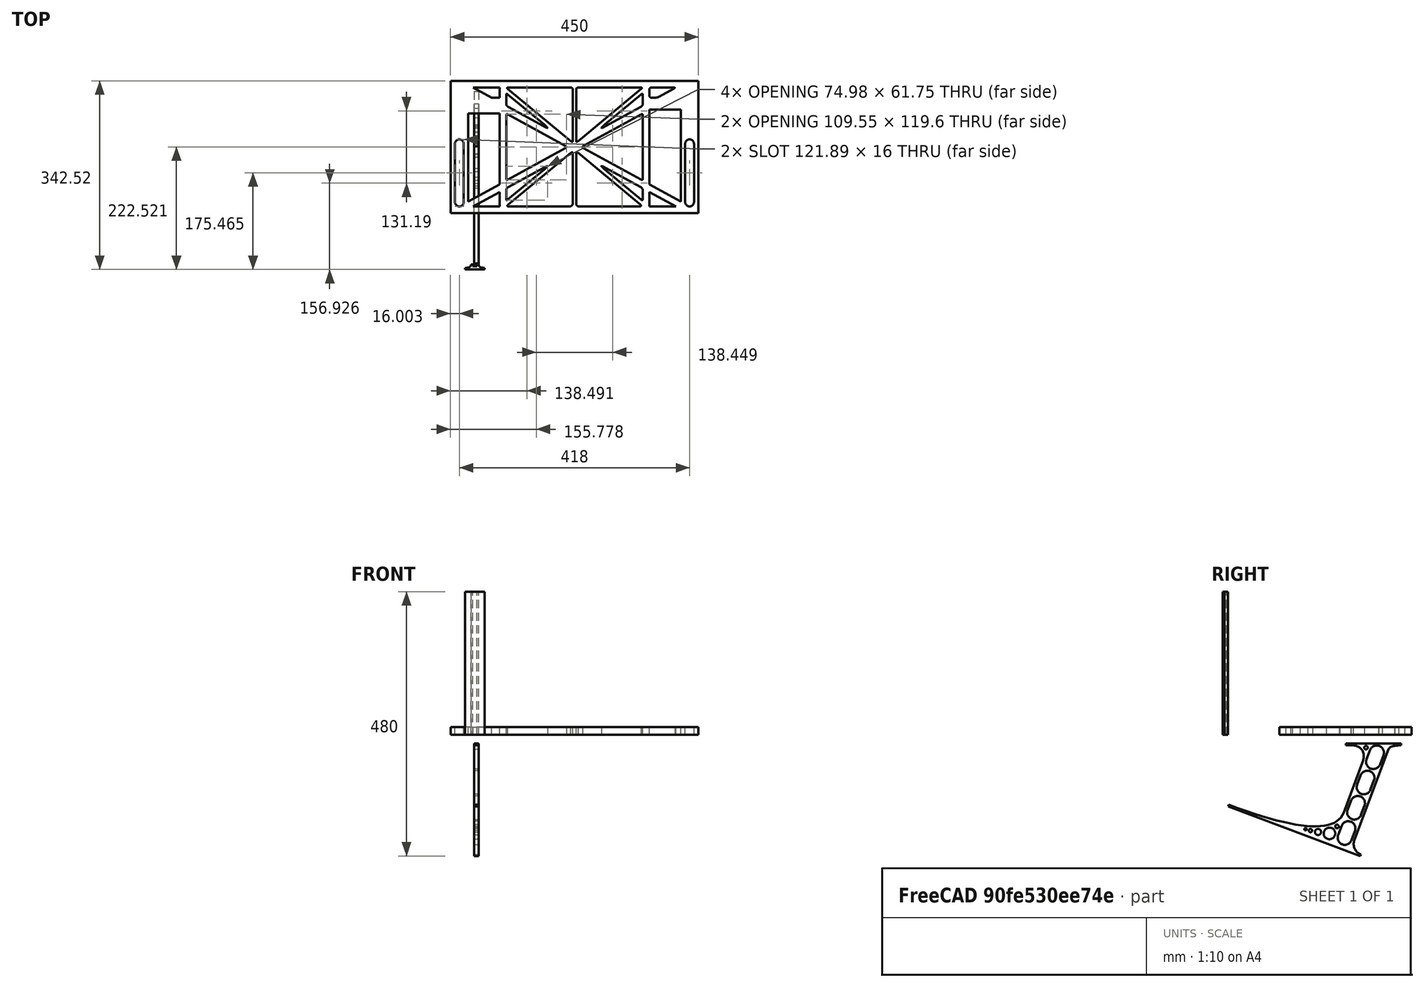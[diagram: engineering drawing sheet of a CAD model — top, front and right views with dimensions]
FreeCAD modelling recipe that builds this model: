
FCSTD DOCUMENT  (FreeCAD 0.19R0.19.2)
Label: laptopStand102
License: All rights reserved
LicenseURL: http://en.wikipedia.org/wiki/All_rights_reserved
objects: Sketcher::SketchObject×3, Part::Extrusion×3
note: 6 computed .brp shape members not serialized (recipe doc carries the construction recipe); baked Part::Feature solids carry a one-line shape summary decoded from their .brp

FEATURE [Sketcher::SketchObject] Sketch
  FullyConstrained = false
  sketch-geometry (276):
    g0: LineSegment StartX=-10.9272 StartY=-82.7794 StartZ=0 EndX=46.0728 EndY=-51.4823 EndZ=0
    g1: LineSegment StartX=366.073 StartY=-91.7794 StartZ=0 EndX=318.073 EndY=-65.424 EndZ=0
    g2: LineSegment StartX=-10.9272 StartY=77.3346 StartZ=0 EndX=-10.9272 EndY=-82.7794 EndZ=0
    g3: LineSegment StartX=375.073 StartY=-82.7794 StartZ=0 EndX=375.073 EndY=83.9235 EndZ=0
    g4: LineSegment StartX=-1.92719 StartY=-91.7794 StartZ=0 EndX=46.0728 EndY=-91.7794 EndZ=0
    g5: LineSegment StartX=318.073 StartY=83.9235 StartZ=0 EndX=318.073 EndY=-51.4823 EndZ=0
    g6: LineSegment StartX=318.073 StartY=-51.4823 StartZ=0 EndX=375.073 EndY=-82.7794 EndZ=0
    g7: LineSegment StartX=318.073 StartY=-65.424 StartZ=0 EndX=318.073 EndY=-91.7794 EndZ=0
    g8: LineSegment StartX=318.073 StartY=-91.7794 StartZ=0 EndX=366.073 EndY=-91.7794 EndZ=0
    g9: LineSegment StartX=46.0728 StartY=-65.424 StartZ=0 EndX=-1.92719 EndY=-91.7794 EndZ=0
    g10: LineSegment StartX=46.0728 StartY=-65.424 StartZ=0 EndX=46.0728 EndY=-91.7794 EndZ=0
    g11: LineSegment StartX=46.0728 StartY=77.3346 StartZ=0 EndX=46.0728 EndY=-51.4823 EndZ=0
    g12: LineSegment StartX=-42.9272 StartY=136.221 StartZ=0 EndX=-42.9272 EndY=-103.779 EndZ=0
    g13: LineSegment StartX=407.073 StartY=136.221 StartZ=0 EndX=407.073 EndY=-103.779 EndZ=0
    g14: ArcOfCircle CenterX=-26.9272 CenterY=22.1087 CenterZ=0 NormalX=0 NormalY=0 NormalZ=1 AngleXU=0 Radius=8 StartAngle=1e-16 EndAngle=3.14159
    g15: ArcOfCircle CenterX=-26.9272 CenterY=-83.7794 CenterZ=0 NormalX=0 NormalY=0 NormalZ=1 AngleXU=0 Radius=8 StartAngle=3.14159 EndAngle=6.28319
    g16: LineSegment StartX=-34.9272 StartY=22.1087 StartZ=0 EndX=-34.9272 EndY=-83.7794 EndZ=0
    g17: LineSegment StartX=-18.9272 StartY=22.1087 StartZ=0 EndX=-18.9272 EndY=-83.7794 EndZ=0
    g18: ArcOfCircle CenterX=391.073 CenterY=22.1087 CenterZ=0 NormalX=0 NormalY=0 NormalZ=1 AngleXU=0 Radius=8 StartAngle=-4.4e-15 EndAngle=3.14159
    g19: LineSegment StartX=399.073 StartY=22.1087 StartZ=0 EndX=399.073 EndY=-83.7794 EndZ=0
    g20: LineSegment StartX=383.073 StartY=22.1087 StartZ=0 EndX=383.073 EndY=-83.7794 EndZ=0
    g21: ArcOfCircle CenterX=391.073 CenterY=-83.7794 CenterZ=0 NormalX=0 NormalY=0 NormalZ=1 AngleXU=0 Radius=8 StartAngle=3.14159 EndAngle=6.28319
    g22: Circle CenterX=175.022 CenterY=27.0628 CenterZ=0 NormalX=0 NormalY=0 NormalZ=1 AngleXU=0 Radius=1
    g23: Circle CenterX=179.022 CenterY=24.8665 CenterZ=0 NormalX=0 NormalY=0 NormalZ=1 AngleXU=0 Radius=1
    g24: Circle CenterX=179.022 CenterY=27.0628 CenterZ=0 NormalX=0 NormalY=0 NormalZ=1 AngleXU=0 Radius=1
    g25: BSplineCurve PolesCount=3 KnotsCount=2 Degree=2 IsPeriodic=0
    g26: GeomPoint X=175.022 Y=27.0628 Z=0
    g27: GeomPoint X=179.022 Y=27.0628 Z=0
    g28: Circle CenterX=189.124 CenterY=27.0628 CenterZ=0 NormalX=0 NormalY=0 NormalZ=1 AngleXU=0 Radius=1
    g29: Circle CenterX=185.124 CenterY=24.8665 CenterZ=0 NormalX=0 NormalY=0 NormalZ=1 AngleXU=0 Radius=1
    g30: Circle CenterX=185.124 CenterY=27.0628 CenterZ=0 NormalX=0 NormalY=0 NormalZ=1 AngleXU=0 Radius=1
    g31: BSplineCurve PolesCount=3 KnotsCount=2 Degree=2 IsPeriodic=0
    g32: GeomPoint X=189.124 Y=27.0628 Z=0
    g33: GeomPoint X=185.124 Y=27.0628 Z=0
    g34: Circle CenterX=175.022 CenterY=5.37834 CenterZ=0 NormalX=0 NormalY=0 NormalZ=1 AngleXU=0 Radius=1
    g35: Circle CenterX=179.022 CenterY=7.57463 CenterZ=0 NormalX=0 NormalY=0 NormalZ=1 AngleXU=0 Radius=1
    g36: Circle CenterX=179.022 CenterY=5.34704 CenterZ=0 NormalX=0 NormalY=0 NormalZ=1 AngleXU=0 Radius=1
    g37: BSplineCurve PolesCount=3 KnotsCount=2 Degree=2 IsPeriodic=0
    g38: GeomPoint X=175.022 Y=5.37834 Z=0
    g39: GeomPoint X=179.022 Y=5.34704 Z=0
    g40: Circle CenterX=189.124 CenterY=5.37834 CenterZ=0 NormalX=0 NormalY=0 NormalZ=1 AngleXU=0 Radius=1
    g41: Circle CenterX=185.124 CenterY=7.57463 CenterZ=0 NormalX=0 NormalY=0 NormalZ=1 AngleXU=0 Radius=1
    g42: Circle CenterX=185.124 CenterY=5.34704 CenterZ=0 NormalX=0 NormalY=0 NormalZ=1 AngleXU=0 Radius=1
    g43: BSplineCurve PolesCount=3 KnotsCount=2 Degree=2 IsPeriodic=0
    g44: GeomPoint X=189.124 Y=5.37834 Z=0
    g45: GeomPoint X=185.124 Y=5.34704 Z=0
    g46: Circle CenterX=165.871 CenterY=18.1458 CenterZ=0 NormalX=0 NormalY=0 NormalZ=1 AngleXU=0 Radius=1
    g47: Circle CenterX=169.377 CenterY=16.2206 CenterZ=0 NormalX=0 NormalY=0 NormalZ=1 AngleXU=0 Radius=1
    g48: Circle CenterX=165.871 CenterY=14.2954 CenterZ=0 NormalX=0 NormalY=0 NormalZ=1 AngleXU=0 Radius=1
    g49: BSplineCurve PolesCount=3 KnotsCount=2 Degree=2 IsPeriodic=0
    g50: GeomPoint X=165.871 Y=18.1458 Z=0
    g51: GeomPoint X=165.871 Y=14.2954 Z=0
    g52: Circle CenterX=198.275 CenterY=18.1458 CenterZ=0 NormalX=0 NormalY=0 NormalZ=1 AngleXU=0 Radius=1
    g53: Circle CenterX=194.768 CenterY=16.2206 CenterZ=0 NormalX=0 NormalY=0 NormalZ=1 AngleXU=0 Radius=1
    g54: Circle CenterX=198.275 CenterY=14.2954 CenterZ=0 NormalX=0 NormalY=0 NormalZ=1 AngleXU=0 Radius=1
    g55: BSplineCurve PolesCount=3 KnotsCount=2 Degree=2 IsPeriodic=0
    g56: GeomPoint X=198.275 Y=18.1458 Z=0
    g57: GeomPoint X=198.275 Y=14.2954 Z=0
    g58: LineSegment StartX=407.073 StartY=-103.779 StartZ=0 EndX=-42.9272 EndY=-103.779 EndZ=0
    g59: LineSegment StartX=407.073 StartY=136.221 StartZ=0 EndX=-42.9272 EndY=136.221 EndZ=0
    g60: LineSegment StartX=46.0728 StartY=77.3346 StartZ=0 EndX=-10.9272 EndY=77.3346 EndZ=0
    g61: LineSegment StartX=46.0728 StartY=105.865 StartZ=0 EndX=31.5028 EndY=105.865 EndZ=0
    g62: LineSegment StartX=46.0728 StartY=124.221 StartZ=0 EndX=46.0728 EndY=105.865 EndZ=0
    g63: LineSegment StartX=-1.92719 StartY=124.221 StartZ=0 EndX=31.5028 EndY=105.865 EndZ=0
    g64: LineSegment StartX=46.0728 StartY=124.221 StartZ=0 EndX=-1.92719 EndY=124.221 EndZ=0
    g65: LineSegment StartX=318.073 StartY=83.9235 StartZ=0 EndX=375.073 EndY=83.9235 EndZ=0
    g66: Circle CenterX=125.607 CenterY=54.1951 CenterZ=0 NormalX=0 NormalY=0 NormalZ=1 AngleXU=0 Radius=1
    g67: Circle CenterX=139.632 CenterY=46.4944 CenterZ=0 NormalX=0 NormalY=0 NormalZ=1 AngleXU=0 Radius=1
    g68: Circle CenterX=127.326 CenterY=56.7187 CenterZ=0 NormalX=0 NormalY=0 NormalZ=1 AngleXU=0 Radius=1
    g69: BSplineCurve PolesCount=3 KnotsCount=2 Degree=2 IsPeriodic=0
    g70: GeomPoint X=125.607 Y=54.1951 Z=0
    g71: GeomPoint X=127.326 Y=56.7187 Z=0
    g72: Circle CenterX=236.821 CenterY=56.7187 CenterZ=0 NormalX=0 NormalY=0 NormalZ=1 AngleXU=0 Radius=1
    g73: Circle CenterX=224.513 CenterY=46.4944 CenterZ=0 NormalX=0 NormalY=0 NormalZ=1 AngleXU=0 Radius=1
    g74: Circle CenterX=238.538 CenterY=54.1951 CenterZ=0 NormalX=0 NormalY=0 NormalZ=1 AngleXU=0 Radius=1
    g75: BSplineCurve PolesCount=3 KnotsCount=2 Degree=2 IsPeriodic=0
    g76: GeomPoint X=236.821 Y=56.7187 Z=0
    g77: GeomPoint X=238.538 Y=54.1951 Z=0
    g78: Circle CenterX=238.538 CenterY=-21.7539 CenterZ=0 NormalX=0 NormalY=0 NormalZ=1 AngleXU=0 Radius=1
    g79: Circle CenterX=224.513 CenterY=-14.0532 CenterZ=0 NormalX=0 NormalY=0 NormalZ=1 AngleXU=0 Radius=1
    g80: Circle CenterX=236.821 CenterY=-24.2775 CenterZ=0 NormalX=0 NormalY=0 NormalZ=1 AngleXU=0 Radius=1
    g81: BSplineCurve PolesCount=3 KnotsCount=2 Degree=2 IsPeriodic=0
    g82: GeomPoint X=238.538 Y=-21.7539 Z=0
    g83: GeomPoint X=236.821 Y=-24.2775 Z=0
    g84: Circle CenterX=125.607 CenterY=-21.7539 CenterZ=0 NormalX=0 NormalY=0 NormalZ=1 AngleXU=0 Radius=1
    g85: Circle CenterX=139.632 CenterY=-14.0532 CenterZ=0 NormalX=0 NormalY=0 NormalZ=1 AngleXU=0 Radius=1
    g86: Circle CenterX=127.325 CenterY=-24.2775 CenterZ=0 NormalX=0 NormalY=0 NormalZ=1 AngleXU=0 Radius=1
    g87: BSplineCurve PolesCount=3 KnotsCount=2 Degree=2 IsPeriodic=0
    g88: GeomPoint X=125.607 Y=-21.7539 Z=0
    g89: GeomPoint X=127.325 Y=-24.2775 Z=0
    g90: Circle CenterX=302.996 CenterY=111.695 CenterZ=0 NormalX=0 NormalY=0 NormalZ=1 AngleXU=0 Radius=1
    g91: Circle CenterX=306.073 CenterY=114.251 CenterZ=0 NormalX=0 NormalY=0 NormalZ=1 AngleXU=0 Radius=1
    g92: Circle CenterX=306.073 CenterY=110.251 CenterZ=0 NormalX=0 NormalY=0 NormalZ=1 AngleXU=0 Radius=1
    g93: BSplineCurve PolesCount=3 KnotsCount=2 Degree=2 IsPeriodic=0
    g94: GeomPoint X=302.996 Y=111.695 Z=0
    g95: GeomPoint X=306.073 Y=110.251 Z=0
    g96: Circle CenterX=306.073 CenterY=95.2763 CenterZ=0 NormalX=0 NormalY=0 NormalZ=1 AngleXU=0 Radius=1
    g97: Circle CenterX=306.073 CenterY=91.2763 CenterZ=0 NormalX=0 NormalY=0 NormalZ=1 AngleXU=0 Radius=1
    g98: Circle CenterX=302.567 CenterY=89.3511 CenterZ=0 NormalX=0 NormalY=0 NormalZ=1 AngleXU=0 Radius=1
    g99: BSplineCurve PolesCount=3 KnotsCount=2 Degree=2 IsPeriodic=0
    g100: GeomPoint X=306.073 Y=95.2763 Z=0
    g101: GeomPoint X=302.567 Y=89.3511 Z=0
    g102: LineSegment StartX=306.073 StartY=110.251 StartZ=0 EndX=306.073 EndY=95.2763 EndZ=0
    g103: LineSegment StartX=302.996 StartY=111.695 StartZ=0 EndX=236.821 EndY=56.7187 EndZ=0
    g104: LineSegment StartX=238.538 StartY=54.1951 StartZ=0 EndX=302.567 EndY=89.3511 EndZ=0
    g105: Circle CenterX=61.1496 CenterY=111.695 CenterZ=0 NormalX=0 NormalY=0 NormalZ=1 AngleXU=0 Radius=1
    g106: Circle CenterX=58.0728 CenterY=114.251 CenterZ=0 NormalX=0 NormalY=0 NormalZ=1 AngleXU=0 Radius=1
    g107: Circle CenterX=58.0728 CenterY=110.251 CenterZ=0 NormalX=0 NormalY=0 NormalZ=1 AngleXU=0 Radius=1
    g108: BSplineCurve PolesCount=3 KnotsCount=2 Degree=2 IsPeriodic=0
    g109: GeomPoint X=61.1496 Y=111.695 Z=0
    g110: GeomPoint X=58.0728 Y=110.251 Z=0
    g111: Circle CenterX=61.5791 CenterY=89.3511 CenterZ=0 NormalX=0 NormalY=0 NormalZ=1 AngleXU=0 Radius=1
    g112: Circle CenterX=58.0728 CenterY=91.2763 CenterZ=0 NormalX=0 NormalY=0 NormalZ=1 AngleXU=0 Radius=1
    g113: Circle CenterX=58.0728 CenterY=95.2763 CenterZ=0 NormalX=0 NormalY=0 NormalZ=1 AngleXU=0 Radius=1
    g114: BSplineCurve PolesCount=3 KnotsCount=2 Degree=2 IsPeriodic=0
    g115: GeomPoint X=61.5791 Y=89.3511 Z=0
    g116: GeomPoint X=58.0728 Y=95.2763 Z=0
    g117: LineSegment StartX=58.0728 StartY=110.251 StartZ=0 EndX=58.0728 EndY=95.2763 EndZ=0
    g118: LineSegment StartX=61.1496 StartY=111.695 StartZ=0 EndX=127.326 EndY=56.7187 EndZ=0
    g119: LineSegment StartX=125.607 StartY=54.1951 StartZ=0 EndX=61.5791 EndY=89.3511 EndZ=0
    g120: Circle CenterX=61.5791 CenterY=-56.9099 CenterZ=0 NormalX=0 NormalY=0 NormalZ=1 AngleXU=0 Radius=1
    g121: Circle CenterX=58.0728 CenterY=-58.8351 CenterZ=0 NormalX=0 NormalY=0 NormalZ=1 AngleXU=0 Radius=1
    g122: Circle CenterX=58.0728 CenterY=-62.8351 CenterZ=0 NormalX=0 NormalY=0 NormalZ=1 AngleXU=0 Radius=1
    g123: BSplineCurve PolesCount=3 KnotsCount=2 Degree=2 IsPeriodic=0
    g124: GeomPoint X=61.5791 Y=-56.9099 Z=0
    g125: GeomPoint X=58.0728 Y=-62.8351 Z=0
    g126: Circle CenterX=58.0728 CenterY=-77.8102 CenterZ=0 NormalX=0 NormalY=0 NormalZ=1 AngleXU=0 Radius=1
    g127: Circle CenterX=58.0728 CenterY=-81.8102 CenterZ=0 NormalX=0 NormalY=0 NormalZ=1 AngleXU=0 Radius=1
    g128: Circle CenterX=61.1496 CenterY=-79.2541 CenterZ=0 NormalX=0 NormalY=0 NormalZ=1 AngleXU=0 Radius=1
    g129: BSplineCurve PolesCount=3 KnotsCount=2 Degree=2 IsPeriodic=0
    g130: GeomPoint X=58.0728 Y=-77.8102 Z=0
    g131: GeomPoint X=61.1496 Y=-79.2541 Z=0
    g132: LineSegment StartX=58.0728 StartY=-62.8351 StartZ=0 EndX=58.0728 EndY=-77.8102 EndZ=0
    g133: LineSegment StartX=61.1496 StartY=-79.2541 StartZ=0 EndX=127.325 EndY=-24.2775 EndZ=0
    g134: LineSegment StartX=125.607 StartY=-21.7539 StartZ=0 EndX=61.5791 EndY=-56.9099 EndZ=0
    g135: Circle CenterX=302.567 CenterY=-56.9099 CenterZ=0 NormalX=0 NormalY=0 NormalZ=1 AngleXU=0 Radius=1
    g136: Circle CenterX=306.073 CenterY=-58.8351 CenterZ=0 NormalX=0 NormalY=0 NormalZ=1 AngleXU=0 Radius=1
    g137: Circle CenterX=306.073 CenterY=-62.8351 CenterZ=0 NormalX=0 NormalY=0 NormalZ=1 AngleXU=0 Radius=1
    g138: BSplineCurve PolesCount=3 KnotsCount=2 Degree=2 IsPeriodic=0
    g139: GeomPoint X=302.567 Y=-56.9099 Z=0
    g140: GeomPoint X=306.073 Y=-62.8351 Z=0
    g141: Circle CenterX=302.996 CenterY=-79.2541 CenterZ=0 NormalX=0 NormalY=0 NormalZ=1 AngleXU=0 Radius=1
    g142: Circle CenterX=306.073 CenterY=-81.8102 CenterZ=0 NormalX=0 NormalY=0 NormalZ=1 AngleXU=0 Radius=1
    g143: Circle CenterX=306.073 CenterY=-77.8102 CenterZ=0 NormalX=0 NormalY=0 NormalZ=1 AngleXU=0 Radius=1
    g144: BSplineCurve PolesCount=3 KnotsCount=2 Degree=2 IsPeriodic=0
    g145: GeomPoint X=302.996 Y=-79.2541 Z=0
    g146: GeomPoint X=306.073 Y=-77.8102 Z=0
    g147: LineSegment StartX=306.073 StartY=-62.8351 StartZ=0 EndX=306.073 EndY=-77.8102 EndZ=0
    g148: LineSegment StartX=302.996 StartY=-79.2541 StartZ=0 EndX=236.821 EndY=-24.2775 EndZ=0
    g149: LineSegment StartX=238.538 StartY=-21.7539 StartZ=0 EndX=302.567 EndY=-56.9099 EndZ=0
    g150: Circle CenterX=61.6457 CenterY=-88.8112 CenterZ=0 NormalX=0 NormalY=0 NormalZ=1 AngleXU=0 Radius=1
    g151: Circle CenterX=58.0728 CenterY=-91.7794 CenterZ=0 NormalX=0 NormalY=0 NormalZ=1 AngleXU=0 Radius=1
    g152: Circle CenterX=63.9135 CenterY=-91.7794 CenterZ=0 NormalX=0 NormalY=0 NormalZ=1 AngleXU=0 Radius=1
    g153: BSplineCurve PolesCount=3 KnotsCount=2 Degree=2 IsPeriodic=0
    g154: GeomPoint X=61.6457 Y=-88.8112 Z=0
    g155: GeomPoint X=63.9135 Y=-91.7794 Z=0
    g156: Circle CenterX=179.022 CenterY=-85.8163 CenterZ=0 NormalX=0 NormalY=0 NormalZ=1 AngleXU=0 Radius=1
    g157: Circle CenterX=179.022 CenterY=-91.7794 CenterZ=0 NormalX=0 NormalY=0 NormalZ=1 AngleXU=0 Radius=1
    g158: Circle CenterX=171.895 CenterY=-91.7794 CenterZ=0 NormalX=0 NormalY=0 NormalZ=1 AngleXU=0 Radius=1
    g159: BSplineCurve PolesCount=3 KnotsCount=2 Degree=2 IsPeriodic=0
    g160: GeomPoint X=179.022 Y=-85.8163 Z=0
    g161: GeomPoint X=171.895 Y=-91.7794 Z=0
    g162: Circle CenterX=185.124 CenterY=-86.2028 CenterZ=0 NormalX=0 NormalY=0 NormalZ=1 AngleXU=0 Radius=1
    g163: Circle CenterX=185.124 CenterY=-91.7794 CenterZ=0 NormalX=0 NormalY=0 NormalZ=1 AngleXU=0 Radius=1
    g164: Circle CenterX=191.747 CenterY=-91.7794 CenterZ=0 NormalX=0 NormalY=0 NormalZ=1 AngleXU=0 Radius=1
    g165: BSplineCurve PolesCount=3 KnotsCount=2 Degree=2 IsPeriodic=0
    g166: GeomPoint X=185.124 Y=-86.2028 Z=0
    g167: GeomPoint X=191.747 Y=-91.7794 Z=0
    g168: Circle CenterX=299.888 CenterY=-86.6413 CenterZ=0 NormalX=0 NormalY=0 NormalZ=1 AngleXU=0 Radius=1
    g169: Circle CenterX=306.073 CenterY=-91.7794 CenterZ=0 NormalX=0 NormalY=0 NormalZ=1 AngleXU=0 Radius=1
    g170: Circle CenterX=298.776 CenterY=-91.7794 CenterZ=0 NormalX=0 NormalY=0 NormalZ=1 AngleXU=0 Radius=1
    g171: BSplineCurve PolesCount=3 KnotsCount=2 Degree=2 IsPeriodic=0
    g172: GeomPoint X=299.888 Y=-86.6413 Z=0
    g173: GeomPoint X=298.776 Y=-91.7794 Z=0
    g174: LineSegment StartX=189.124 StartY=5.37834 StartZ=0 EndX=299.888 EndY=-86.6413 EndZ=0
    g175: LineSegment StartX=298.776 StartY=-91.7794 StartZ=0 EndX=191.747 EndY=-91.7794 EndZ=0
    g176: LineSegment StartX=185.124 StartY=-86.2028 StartZ=0 EndX=185.124 EndY=5.34704 EndZ=0
    g177: LineSegment StartX=179.022 StartY=5.34704 StartZ=0 EndX=179.022 EndY=-85.8163 EndZ=0
    g178: LineSegment StartX=171.895 StartY=-91.7794 StartZ=0 EndX=63.9135 EndY=-91.7794 EndZ=0
    g179: LineSegment StartX=61.6457 StartY=-88.8112 StartZ=0 EndX=175.022 EndY=5.37834 EndZ=0
    g180: Circle CenterX=302.073 CenterY=124.221 CenterZ=0 NormalX=0 NormalY=0 NormalZ=1 AngleXU=0 Radius=1
    g181: Circle CenterX=306.073 CenterY=124.221 CenterZ=0 NormalX=0 NormalY=0 NormalZ=1 AngleXU=0 Radius=1
    g182: Circle CenterX=302.996 CenterY=121.665 CenterZ=0 NormalX=0 NormalY=0 NormalZ=1 AngleXU=0 Radius=1
    g183: BSplineCurve PolesCount=3 KnotsCount=2 Degree=2 IsPeriodic=0
    g184: GeomPoint X=302.073 Y=124.221 Z=0
    g185: GeomPoint X=302.996 Y=121.665 Z=0
    g186: Circle CenterX=189.124 CenterY=124.221 CenterZ=0 NormalX=0 NormalY=0 NormalZ=1 AngleXU=0 Radius=1
    g187: Circle CenterX=185.124 CenterY=124.221 CenterZ=0 NormalX=0 NormalY=0 NormalZ=1 AngleXU=0 Radius=1
    g188: Circle CenterX=185.124 CenterY=120.221 CenterZ=0 NormalX=0 NormalY=0 NormalZ=1 AngleXU=0 Radius=1
    g189: BSplineCurve PolesCount=3 KnotsCount=2 Degree=2 IsPeriodic=0
    g190: GeomPoint X=189.124 Y=124.221 Z=0
    g191: GeomPoint X=185.124 Y=120.221 Z=0
    g192: Circle CenterX=175.022 CenterY=124.221 CenterZ=0 NormalX=0 NormalY=0 NormalZ=1 AngleXU=0 Radius=1
    g193: Circle CenterX=179.022 CenterY=124.221 CenterZ=0 NormalX=0 NormalY=0 NormalZ=1 AngleXU=0 Radius=1
    g194: Circle CenterX=179.022 CenterY=120.221 CenterZ=0 NormalX=0 NormalY=0 NormalZ=1 AngleXU=0 Radius=1
    g195: BSplineCurve PolesCount=3 KnotsCount=2 Degree=2 IsPeriodic=0
    g196: GeomPoint X=175.022 Y=124.221 Z=0
    g197: GeomPoint X=179.022 Y=120.221 Z=0
    g198: Circle CenterX=62.0728 CenterY=124.221 CenterZ=0 NormalX=0 NormalY=0 NormalZ=1 AngleXU=0 Radius=1
    g199: Circle CenterX=58.0728 CenterY=124.221 CenterZ=0 NormalX=0 NormalY=0 NormalZ=1 AngleXU=0 Radius=1
    g200: Circle CenterX=61.1496 CenterY=121.665 CenterZ=0 NormalX=0 NormalY=0 NormalZ=1 AngleXU=0 Radius=1
    g201: BSplineCurve PolesCount=3 KnotsCount=2 Degree=2 IsPeriodic=0
    g202: GeomPoint X=62.0728 Y=124.221 Z=0
    g203: GeomPoint X=61.1496 Y=121.665 Z=0
    g204: LineSegment StartX=62.0728 StartY=124.221 StartZ=0 EndX=175.022 EndY=124.221 EndZ=0
    g205: LineSegment StartX=179.022 StartY=120.221 StartZ=0 EndX=179.022 EndY=27.0628 EndZ=0
    g206: LineSegment StartX=185.124 StartY=27.0628 StartZ=0 EndX=185.124 EndY=120.221 EndZ=0
    g207: LineSegment StartX=189.124 StartY=124.221 StartZ=0 EndX=302.073 EndY=124.221 EndZ=0
    g208: LineSegment StartX=302.996 StartY=121.665 StartZ=0 EndX=189.124 EndY=27.0628 EndZ=0
    g209: LineSegment StartX=175.022 StartY=27.0628 StartZ=0 EndX=61.1496 EndY=121.665 EndZ=0
    g210: Circle CenterX=61.5791 CenterY=75.4095 CenterZ=0 NormalX=0 NormalY=0 NormalZ=1 AngleXU=0 Radius=1
    g211: Circle CenterX=58.0728 CenterY=77.3346 CenterZ=0 NormalX=0 NormalY=0 NormalZ=1 AngleXU=0 Radius=1
    g212: Circle CenterX=58.0728 CenterY=73.3346 CenterZ=0 NormalX=0 NormalY=0 NormalZ=1 AngleXU=0 Radius=1
    g213: BSplineCurve PolesCount=3 KnotsCount=2 Degree=2 IsPeriodic=0
    g214: GeomPoint X=61.5791 Y=75.4095 Z=0
    g215: GeomPoint X=58.0728 Y=73.3346 Z=0
    g216: Circle CenterX=58.0728 CenterY=-40.8935 CenterZ=0 NormalX=0 NormalY=0 NormalZ=1 AngleXU=0 Radius=1
    g217: Circle CenterX=58.0728 CenterY=-44.8935 CenterZ=0 NormalX=0 NormalY=0 NormalZ=1 AngleXU=0 Radius=1
    g218: Circle CenterX=61.5791 CenterY=-42.9683 CenterZ=0 NormalX=0 NormalY=0 NormalZ=1 AngleXU=0 Radius=1
    g219: BSplineCurve PolesCount=3 KnotsCount=2 Degree=2 IsPeriodic=0
    g220: GeomPoint X=58.0728 Y=-40.8935 Z=0
    g221: GeomPoint X=61.5791 Y=-42.9683 Z=0
    g222: LineSegment StartX=61.5791 StartY=-42.9683 StartZ=0 EndX=165.871 EndY=14.2954 EndZ=0
    g223: LineSegment StartX=165.871 StartY=18.1458 StartZ=0 EndX=61.5791 EndY=75.4095 EndZ=0
    g224: LineSegment StartX=58.0728 StartY=73.3346 StartZ=0 EndX=58.0728 EndY=-40.8935 EndZ=0
    g225: Circle CenterX=302.567 CenterY=-42.9683 CenterZ=0 NormalX=0 NormalY=0 NormalZ=1 AngleXU=0 Radius=1
    g226: Circle CenterX=306.073 CenterY=-44.8935 CenterZ=0 NormalX=0 NormalY=0 NormalZ=1 AngleXU=0 Radius=1
    g227: Circle CenterX=306.073 CenterY=-40.8935 CenterZ=0 NormalX=0 NormalY=0 NormalZ=1 AngleXU=0 Radius=1
    g228: BSplineCurve PolesCount=3 KnotsCount=2 Degree=2 IsPeriodic=0
    g229: GeomPoint X=302.567 Y=-42.9683 Z=0
    g230: GeomPoint X=306.073 Y=-40.8935 Z=0
    g231: Circle CenterX=306.073 CenterY=73.3346 CenterZ=0 NormalX=0 NormalY=0 NormalZ=1 AngleXU=0 Radius=1
    g232: Circle CenterX=306.073 CenterY=77.3346 CenterZ=0 NormalX=0 NormalY=0 NormalZ=1 AngleXU=0 Radius=1
    g233: Circle CenterX=302.567 CenterY=75.4095 CenterZ=0 NormalX=0 NormalY=0 NormalZ=1 AngleXU=0 Radius=1
    g234: BSplineCurve PolesCount=3 KnotsCount=2 Degree=2 IsPeriodic=0
    g235: GeomPoint X=306.073 Y=73.3346 Z=0
    g236: GeomPoint X=302.567 Y=75.4095 Z=0
    g237: LineSegment StartX=302.567 StartY=-42.9683 StartZ=0 EndX=198.275 EndY=14.2954 EndZ=0
    g238: LineSegment StartX=198.275 StartY=18.1458 StartZ=0 EndX=302.567 EndY=75.4095 EndZ=0
    g239: LineSegment StartX=306.073 StartY=73.3346 StartZ=0 EndX=306.073 EndY=-40.8935 EndZ=0
    g240: LineSegment StartX=322.073 StartY=105.865 StartZ=0 EndX=328.643 EndY=105.865 EndZ=0
    g241: LineSegment StartX=318.073 StartY=120.221 StartZ=0 EndX=318.073 EndY=109.865 EndZ=0
    g242: LineSegment StartX=336.157 StartY=107.779 StartZ=0 EndX=362.567 EndY=122.294 EndZ=0
    g243: Circle CenterX=362.073 CenterY=124.221 CenterZ=0 NormalX=0 NormalY=0 NormalZ=1 AngleXU=0 Radius=1
    g244: Circle CenterX=366.073 CenterY=124.221 CenterZ=0 NormalX=0 NormalY=0 NormalZ=1 AngleXU=0 Radius=1
    g245: Circle CenterX=362.567 CenterY=122.294 CenterZ=0 NormalX=0 NormalY=0 NormalZ=1 AngleXU=0 Radius=1
    g246: BSplineCurve PolesCount=3 KnotsCount=2 Degree=2 IsPeriodic=0
    g247: GeomPoint X=362.073 Y=124.221 Z=0
    g248: GeomPoint X=362.567 Y=122.294 Z=0
    g249: Circle CenterX=322.073 CenterY=124.221 CenterZ=0 NormalX=0 NormalY=0 NormalZ=1 AngleXU=0 Radius=1
    g250: Circle CenterX=318.073 CenterY=124.221 CenterZ=0 NormalX=0 NormalY=0 NormalZ=1 AngleXU=0 Radius=1
    g251: Circle CenterX=318.073 CenterY=120.221 CenterZ=0 NormalX=0 NormalY=0 NormalZ=1 AngleXU=0 Radius=1
    g252: BSplineCurve PolesCount=3 KnotsCount=2 Degree=2 IsPeriodic=0
    g253: GeomPoint X=322.073 Y=124.221 Z=0
    g254: GeomPoint X=318.073 Y=120.221 Z=0
    g255: Circle CenterX=322.073 CenterY=105.865 CenterZ=0 NormalX=0 NormalY=0 NormalZ=1 AngleXU=0 Radius=1
    g256: Circle CenterX=318.073 CenterY=105.865 CenterZ=0 NormalX=0 NormalY=0 NormalZ=1 AngleXU=0 Radius=1
    g257: Circle CenterX=318.073 CenterY=109.865 CenterZ=0 NormalX=0 NormalY=0 NormalZ=1 AngleXU=0 Radius=1
    g258: BSplineCurve PolesCount=3 KnotsCount=2 Degree=2 IsPeriodic=0
    g259: GeomPoint X=322.073 Y=105.865 Z=0
    g260: GeomPoint X=318.073 Y=109.865 Z=0
    g261: Circle CenterX=336.157 CenterY=107.779 CenterZ=0 NormalX=0 NormalY=0 NormalZ=1 AngleXU=0 Radius=1
    g262: Circle CenterX=332.651 CenterY=105.853 CenterZ=0 NormalX=0 NormalY=0 NormalZ=1 AngleXU=0 Radius=1
    g263: Circle CenterX=328.643 CenterY=105.865 CenterZ=0 NormalX=0 NormalY=0 NormalZ=1 AngleXU=0 Radius=1
    g264: BSplineCurve PolesCount=3 KnotsCount=2 Degree=2 IsPeriodic=0
    g265: GeomPoint X=336.157 Y=107.779 Z=0
    g266: GeomPoint X=328.643 Y=105.865 Z=0
    g267: LineSegment StartX=322.073 StartY=124.221 StartZ=0 EndX=362.073 EndY=124.221 EndZ=0
    g268: LineSegment StartX=318.073 StartY=83.9235 StartZ=0 EndX=322.073 EndY=83.9235 EndZ=0
    g269: LineSegment StartX=318.073 StartY=83.9235 StartZ=0 EndX=318.073 EndY=79.9235 EndZ=0
    g270: LineSegment StartX=375.073 StartY=83.9235 StartZ=0 EndX=371.073 EndY=83.9235 EndZ=0
    g271: LineSegment StartX=375.073 StartY=83.9235 StartZ=0 EndX=375.073 EndY=79.9235 EndZ=0
    g272: LineSegment StartX=375.073 StartY=-82.7794 StartZ=0 EndX=375.073 EndY=-78.7794 EndZ=0
    g273: LineSegment StartX=374.992 StartY=-82.1866 StartZ=0 EndX=371.485 EndY=-80.2614 EndZ=0
    g274: LineSegment StartX=318.073 StartY=-51.4823 StartZ=0 EndX=321.579 EndY=-53.4075 EndZ=0
    g275: LineSegment StartX=318.073 StartY=-51.4823 StartZ=0 EndX=318.073 EndY=-47.4823 EndZ=0
  constraints (472):
    c: Horizontal(g4)
    c: Coincident(g5,g6)
    c: Coincident(g7,g1)
    c: Tangent(g5,g7)
    c: Coincident(g10,g9)
    c: Coincident(g0,g11)
    c: Block(g6)
    c: Block(g3)
    c: Block(g1)
    c: Block(g7)
    c: Block(g10)
    c: Block(g9)
    c: Block(g0)
    c: Block(g2)
    c: Block(g8)
    c: Block(g4)
    c: Vertical(g12)
    c: Vertical(g13)
    c: Block(g13)
    c: Block(g12)
    c: Tangent(g14,g17) = 1.5708
    c: Tangent(g14,g16) = -1.5708
    c: Tangent(g16,g15) = -1.5708
    c: Tangent(g17,g15) = 1.5708
    c: Vertical(g16)
    c: Equal(g14,g15)
    c: Block(g17)
    c: Block(g16)
    c: Tangent(g18,g19) = 1.5708
    c: Tangent(g19,g21) = 1.5708
    c: Equal(g18,g21)
    c: Coincident(g20,g18)
    c: Coincident(g20,g21)
    c: Block(g19)
    c: Block(g20)
    c: Weight(g22) = 1
    c: Equal(g22,g23)
    c: Equal(g22,g24)
    c: InternalAlignment(g22,g25)
    c: InternalAlignment(g23,g25)
    c: InternalAlignment(g24,g25)
    c: InternalAlignment(g26,g25)
    c: InternalAlignment(g27,g25)
    c: Weight(g28) = 1
    c: Equal(g28,g29)
    c: Equal(g28,g30)
    c: InternalAlignment(g28,g31)
    c: InternalAlignment(g29,g31)
    c: InternalAlignment(g30,g31)
    c: InternalAlignment(g32,g31)
    c: InternalAlignment(g33,g31)
    c: Block(g31)
    c: Block(g25)
    c: Weight(g34) = 1
    c: Equal(g34,g35)
    c: Equal(g34,g36)
    c: InternalAlignment(g34,g37)
    c: InternalAlignment(g35,g37)
    c: InternalAlignment(g36,g37)
    c: InternalAlignment(g38,g37)
    c: InternalAlignment(g39,g37)
    c: Weight(g40) = 1
    c: Equal(g40,g41)
    c: Equal(g40,g42)
    c: InternalAlignment(g40,g43)
    c: InternalAlignment(g41,g43)
    c: InternalAlignment(g42,g43)
    c: InternalAlignment(g44,g43)
    c: InternalAlignment(g45,g43)
    c: Block(g43)
    c: Block(g37)
    c: Weight(g46) = 1
    c: Equal(g46,g47)
    c: Equal(g46,g48)
    c: InternalAlignment(g46,g49)
    c: InternalAlignment(g47,g49)
    c: InternalAlignment(g48,g49)
    c: InternalAlignment(g50,g49)
    c: InternalAlignment(g51,g49)
    c: Weight(g52) = 1
    c: Equal(g52,g53)
    c: Equal(g52,g54)
    c: InternalAlignment(g52,g55)
    c: InternalAlignment(g53,g55)
    c: InternalAlignment(g54,g55)
    c: InternalAlignment(g56,g55)
    c: InternalAlignment(g57,g55)
    c: Block(g49)
    c: Block(g55)
    c: Coincident(g58,g13)
    c: Coincident(g58,g12)
    c: Horizontal(g58)
    c: Distance(g58) = 450
    c: Coincident(g59,g13)
    c: Coincident(g59,g12)
    c: Horizontal(g59)
    c: Horizontal(g60)
    c: Coincident(g11,g60)
    c: Horizontal(g61)
    c: Vertical(g62)
    c: Block(g62)
    c: Block(g61)
    c: Block(g60)
    c: Distance(g62) = 18.3554
    c: Coincident(g64,g62)
    c: Coincident(g64,g63)
    c: Horizontal(g64)
    c: Block(g64)
    c: Block(g63)
    c: Coincident(g61,g63)
    c: Coincident(g2,g60)
    c: Coincident(g65,g5)
    c: Horizontal(g65)
    c: Block(g65)
    c: Coincident(g3,g65)
    c: Weight(g66) = 1
    c: Equal(g66,g67)
    c: Equal(g66,g68)
    c: InternalAlignment(g66,g69)
    c: InternalAlignment(g67,g69)
    c: InternalAlignment(g68,g69)
    c: InternalAlignment(g70,g69)
    c: InternalAlignment(g71,g69)
    c: Block(g69)
    c: Weight(g72) = 1
    c: Equal(g72,g73)
    c: Equal(g72,g74)
    c: InternalAlignment(g72,g75)
    c: InternalAlignment(g73,g75)
    c: InternalAlignment(g74,g75)
    c: InternalAlignment(g76,g75)
    c: InternalAlignment(g77,g75)
    c: Block(g75)
    c: Weight(g78) = 1
    c: Equal(g78,g79)
    c: Equal(g78,g80)
    c: InternalAlignment(g78,g81)
    c: InternalAlignment(g79,g81)
    c: InternalAlignment(g80,g81)
    c: InternalAlignment(g82,g81)
    c: InternalAlignment(g83,g81)
    c: Block(g81)
    c: Weight(g84) = 1
    c: Equal(g84,g85)
    c: Equal(g84,g86)
    c: InternalAlignment(g84,g87)
    c: InternalAlignment(g85,g87)
    c: InternalAlignment(g86,g87)
    c: InternalAlignment(g88,g87)
    c: InternalAlignment(g89,g87)
    c: Block(g87)
    c: Weight(g90) = 1
    c: Equal(g90,g91)
    c: Equal(g90,g92)
    c: InternalAlignment(g90,g93)
    c: InternalAlignment(g91,g93)
    c: InternalAlignment(g92,g93)
    c: InternalAlignment(g94,g93)
    c: InternalAlignment(g95,g93)
    c: Weight(g96) = 1
    c: Equal(g96,g97)
    c: Equal(g96,g98)
    c: InternalAlignment(g96,g99)
    c: InternalAlignment(g97,g99)
    c: InternalAlignment(g98,g99)
    c: InternalAlignment(g100,g99)
    c: InternalAlignment(g101,g99)
    c: Block(g93)
    c: Block(g99)
    c: Coincident(g102,g93)
    c: Coincident(g102,g99)
    c: Vertical(g102)
    c: Coincident(g103,g93)
    c: Coincident(g103,g75)
    c: Coincident(g104,g75)
    c: Coincident(g104,g99)
    c: Weight(g105) = 1
    c: Equal(g105,g106)
    c: Equal(g105,g107)
    c: InternalAlignment(g105,g108)
    c: InternalAlignment(g106,g108)
    c: InternalAlignment(g107,g108)
    c: InternalAlignment(g109,g108)
    c: InternalAlignment(g110,g108)
    c: Weight(g111) = 1
    c: Equal(g111,g112)
    c: Equal(g111,g113)
    c: InternalAlignment(g111,g114)
    c: InternalAlignment(g112,g114)
    c: InternalAlignment(g113,g114)
    c: InternalAlignment(g115,g114)
    c: InternalAlignment(g116,g114)
    c: Block(g108)
    c: Block(g114)
    c: Coincident(g117,g108)
    c: Coincident(g117,g114)
    c: Vertical(g117)
    c: Coincident(g118,g108)
    c: Coincident(g118,g69)
    c: Coincident(g119,g69)
    c: Coincident(g119,g114)
    c: Weight(g120) = 1
    c: Equal(g120,g121)
    c: Equal(g120,g122)
    c: InternalAlignment(g120,g123)
    c: InternalAlignment(g121,g123)
    c: InternalAlignment(g122,g123)
    c: InternalAlignment(g124,g123)
    c: InternalAlignment(g125,g123)
    c: Weight(g126) = 1
    c: Equal(g126,g127)
    c: Equal(g126,g128)
    c: InternalAlignment(g126,g129)
    c: InternalAlignment(g127,g129)
    c: InternalAlignment(g128,g129)
    c: InternalAlignment(g130,g129)
    c: InternalAlignment(g131,g129)
    c: Block(g123)
    c: Block(g129)
    c: Coincident(g132,g123)
    c: Coincident(g132,g129)
    c: Vertical(g132)
    c: Coincident(g133,g129)
    c: Coincident(g133,g87)
    c: Coincident(g134,g87)
    c: Coincident(g134,g123)
    c: Weight(g135) = 1
    c: Equal(g135,g136)
    c: Equal(g135,g137)
    c: InternalAlignment(g135,g138)
    c: InternalAlignment(g136,g138)
    c: InternalAlignment(g137,g138)
    c: InternalAlignment(g139,g138)
    c: InternalAlignment(g140,g138)
    c: Weight(g141) = 1
    c: Equal(g141,g142)
    c: Equal(g141,g143)
    c: InternalAlignment(g141,g144)
    c: InternalAlignment(g142,g144)
    c: InternalAlignment(g143,g144)
    c: InternalAlignment(g145,g144)
    c: InternalAlignment(g146,g144)
    c: Block(g138)
    c: Block(g144)
    c: Coincident(g147,g138)
    c: Coincident(g147,g144)
    c: Vertical(g147)
    c: Coincident(g148,g144)
    c: Coincident(g148,g81)
    c: Coincident(g149,g81)
    c: Coincident(g149,g138)
    c: Weight(g150) = 1
    c: Equal(g150,g151)
    c: Equal(g150,g152)
    c: InternalAlignment(g150,g153)
    c: InternalAlignment(g151,g153)
    c: InternalAlignment(g152,g153)
    c: InternalAlignment(g154,g153)
    c: InternalAlignment(g155,g153)
    c: Weight(g156) = 1
    c: Equal(g156,g157)
    c: Equal(g156,g158)
    c: InternalAlignment(g156,g159)
    c: InternalAlignment(g157,g159)
    c: InternalAlignment(g158,g159)
    c: InternalAlignment(g160,g159)
    c: InternalAlignment(g161,g159)
    c: Weight(g162) = 1
    c: Equal(g162,g163)
    c: Equal(g162,g164)
    c: InternalAlignment(g162,g165)
    c: InternalAlignment(g163,g165)
    c: InternalAlignment(g164,g165)
    c: InternalAlignment(g166,g165)
    c: InternalAlignment(g167,g165)
    c: Weight(g168) = 1
    c: Equal(g168,g169)
    c: Equal(g168,g170)
    c: InternalAlignment(g168,g171)
    c: InternalAlignment(g169,g171)
    c: InternalAlignment(g170,g171)
    c: InternalAlignment(g172,g171)
    c: InternalAlignment(g173,g171)
    c: Block(g171)
    c: Block(g165)
    c: Block(g159)
    c: Block(g153)
    c: Coincident(g174,g43)
    c: Coincident(g174,g171)
    c: Coincident(g175,g171)
    c: Coincident(g175,g165)
    c: Horizontal(g175)
    c: Coincident(g176,g165)
    c: Coincident(g176,g43)
    c: Vertical(g176)
    c: Coincident(g177,g37)
    c: Coincident(g177,g159)
    c: Vertical(g177)
    c: Coincident(g178,g159)
    c: Coincident(g178,g153)
    c: Horizontal(g178)
    c: Coincident(g179,g153)
    c: Coincident(g179,g37)
    c: Weight(g180) = 1
    c: Equal(g180,g181)
    c: Equal(g180,g182)
    c: InternalAlignment(g180,g183)
    c: InternalAlignment(g181,g183)
    c: InternalAlignment(g182,g183)
    c: InternalAlignment(g184,g183)
    c: InternalAlignment(g185,g183)
    c: Weight(g186) = 1
    c: Equal(g186,g187)
    c: Equal(g186,g188)
    c: InternalAlignment(g186,g189)
    c: InternalAlignment(g187,g189)
    c: InternalAlignment(g188,g189)
    c: InternalAlignment(g190,g189)
    c: InternalAlignment(g191,g189)
    c: Weight(g192) = 1
    c: Equal(g192,g193)
    c: Equal(g192,g194)
    c: InternalAlignment(g192,g195)
    c: InternalAlignment(g193,g195)
    c: InternalAlignment(g194,g195)
    c: InternalAlignment(g196,g195)
    c: InternalAlignment(g197,g195)
    c: Weight(g198) = 1
    c: Equal(g198,g199)
    c: Equal(g198,g200)
    c: InternalAlignment(g198,g201)
    c: InternalAlignment(g199,g201)
    c: InternalAlignment(g200,g201)
    c: InternalAlignment(g202,g201)
    c: InternalAlignment(g203,g201)
    c: Block(g201)
    c: Block(g195)
    c: Block(g189)
    c: Block(g183)
    c: Coincident(g204,g201)
    c: Coincident(g204,g195)
    c: Horizontal(g204)
    c: Coincident(g205,g195)
    c: Coincident(g205,g25)
    c: Vertical(g205)
    c: Coincident(g206,g31)
    c: Coincident(g206,g189)
    c: Vertical(g206)
    c: Coincident(g207,g189)
    c: Coincident(g207,g183)
    c: Horizontal(g207)
    c: Coincident(g208,g183)
    c: Coincident(g208,g31)
    c: Coincident(g209,g25)
    c: Weight(g210) = 1
    c: Equal(g210,g211)
    c: Equal(g210,g212)
    c: InternalAlignment(g210,g213)
    c: InternalAlignment(g211,g213)
    c: InternalAlignment(g212,g213)
    c: InternalAlignment(g214,g213)
    c: InternalAlignment(g215,g213)
    c: Weight(g216) = 1
    c: Equal(g216,g217)
    c: Equal(g216,g218)
    c: InternalAlignment(g216,g219)
    c: InternalAlignment(g217,g219)
    c: InternalAlignment(g218,g219)
    c: InternalAlignment(g220,g219)
    c: InternalAlignment(g221,g219)
    c: Block(g219)
    c: Block(g213)
    c: Coincident(g222,g219)
    c: Coincident(g222,g49)
    c: Coincident(g223,g49)
    c: Coincident(g223,g213)
    c: Coincident(g224,g213)
    c: Coincident(g224,g219)
    c: Vertical(g224)
    c: Weight(g225) = 1
    c: Equal(g225,g226)
    c: Equal(g225,g227)
    c: InternalAlignment(g225,g228)
    c: InternalAlignment(g226,g228)
    c: InternalAlignment(g227,g228)
    c: InternalAlignment(g229,g228)
    c: InternalAlignment(g230,g228)
    c: Weight(g231) = 1
    c: Equal(g231,g232)
    c: Equal(g231,g233)
    c: InternalAlignment(g231,g234)
    c: InternalAlignment(g232,g234)
    c: InternalAlignment(g233,g234)
    c: InternalAlignment(g235,g234)
    c: InternalAlignment(g236,g234)
    c: Block(g234)
    c: Block(g228)
    c: Coincident(g237,g228)
    c: Coincident(g237,g55)
    c: Coincident(g238,g55)
    c: Coincident(g238,g234)
    c: Coincident(g239,g234)
    c: Coincident(g239,g228)
    c: Vertical(g239)
    c: Horizontal(g240)
    c: Block(g240)
    c: Vertical(g241)
    c: Block(g241)
    c: Block(g242)
    c: Weight(g243) = 1
    c: Equal(g243,g244)
    c: Equal(g243,g245)
    c: InternalAlignment(g243,g246)
    c: InternalAlignment(g244,g246)
    c: InternalAlignment(g245,g246)
    c: InternalAlignment(g247,g246)
    c: InternalAlignment(g248,g246)
    c: Weight(g249) = 1
    c: Equal(g249,g250)
    c: Equal(g249,g251)
    c: InternalAlignment(g249,g252)
    c: InternalAlignment(g250,g252)
    c: InternalAlignment(g251,g252)
    c: InternalAlignment(g253,g252)
    c: InternalAlignment(g254,g252)
    c: Weight(g255) = 1
    c: Equal(g255,g256)
    c: Equal(g255,g257)
    c: InternalAlignment(g255,g258)
    c: InternalAlignment(g256,g258)
    c: InternalAlignment(g257,g258)
    c: InternalAlignment(g259,g258)
    c: InternalAlignment(g260,g258)
    c: Weight(g261) = 1
    c: Equal(g261,g262)
    c: Equal(g261,g263)
    c: InternalAlignment(g261,g264)
    c: InternalAlignment(g262,g264)
    c: InternalAlignment(g263,g264)
    c: InternalAlignment(g265,g264)
    c: InternalAlignment(g266,g264)
    c: Block(g246)
    c: Block(g252)
    c: Block(g258)
    c: Block(g264)
    c: Coincident(g267,g252)
    c: Coincident(g267,g246)
    c: Horizontal(g267)
    c: Block(g209)
    c: Horizontal(g268)
    c: Vertical(g269)
    c: Horizontal(g270)
    c: Vertical(g271)
    c: Vertical(g272)
    c: Vertical(g275)
    c: Parallel(g6,g274)
    c: Parallel(g6,g273)
    c: Distance(g273) = 4
    c: Distance(g272) = 4
    c: Distance(g274) = 4
    c: Distance(g275) = 4
    c: Distance(g269) = 4
    c: Distance(g268) = 4
    c: Distance(g271) = 4
    c: Distance(g270) = 4
    c: Coincident(g271,g3)
    c: Coincident(g270,g3)
    c: Coincident(g268,g5)
    c: Coincident(g269,g5)
    c: Coincident(g274,g5)
    c: Coincident(g275,g5)
    c: Coincident(g272,g3)
FEATURE [Sketcher::SketchObject] Sketch001
  FullyConstrained = true
  MapMode = 4
  Placement = pos=(0,0,0) rot=(0.57735,0.57735,0.57735;2.0944rad)
  Support = -> [Sketch]
  sketch-geometry (46):
    g0: BSplineCurve PolesCount=3 KnotsCount=2 Degree=2 IsPeriodic=0
    g1: ArcOfCircle CenterX=73.1223 CenterY=-32.291 CenterZ=0 NormalX=0 NormalY=0 NormalZ=1 AngleXU=0 Radius=13 StartAngle=5.92268 EndAngle=9.06428
    g2: ArcOfCircle CenterX=66.7816 CenterY=-49.1439 CenterZ=0 NormalX=0 NormalY=0 NormalZ=1 AngleXU=0 Radius=13 StartAngle=2.78068 EndAngle=5.92131
    g3: ArcOfCircle CenterX=55.9263 CenterY=-78.1807 CenterZ=0 NormalX=0 NormalY=0 NormalZ=1 AngleXU=0 Radius=13 StartAngle=5.92268 EndAngle=9.06428
    g4: ArcOfCircle CenterX=49.5884 CenterY=-95.0342 CenterZ=0 NormalX=0 NormalY=0 NormalZ=1 AngleXU=0 Radius=13 StartAngle=2.78068 EndAngle=5.92131
    g5: ArcOfCircle CenterX=38.7206 CenterY=-124.067 CenterZ=0 NormalX=0 NormalY=0 NormalZ=1 AngleXU=0 Radius=13 StartAngle=5.92268 EndAngle=9.06428
    g6: ArcOfCircle CenterX=32.3875 CenterY=-140.92 CenterZ=0 NormalX=0 NormalY=0 NormalZ=1 AngleXU=0 Radius=13 StartAngle=2.78068 EndAngle=5.92131
    g7: ArcOfCircle CenterX=21.4715 CenterY=-169.934 CenterZ=0 NormalX=0 NormalY=0 NormalZ=1 AngleXU=0 Radius=13 StartAngle=5.92268 EndAngle=9.06428
    g8: ArcOfCircle CenterX=15.1336 CenterY=-186.787 CenterZ=0 NormalX=0 NormalY=0 NormalZ=1 AngleXU=0 Radius=13 StartAngle=2.78068 EndAngle=5.92131
    g9-g12: Circle x4 (B-spline internal-alignment scaffolding for g13; pole/knot coordinates omitted)
    g13: BSplineCurve PolesCount=4 KnotsCount=2 Degree=3 IsPeriodic=0
    g14: GeomPoint X=28.8094 Y=-19.0875 Z=0
    g15: GeomPoint X=47.0443 Y=-50.4712 Z=0
    g16: Circle CenterX=53.5586 CenterY=-23.2695 CenterZ=0 NormalX=0 NormalY=0 NormalZ=1 AngleXU=0 Radius=3.24518
    g17: Circle CenterX=-195.441 CenterY=-127.082 CenterZ=0 NormalX=0 NormalY=0 NormalZ=1 AngleXU=0 Radius=1
    g18: Circle CenterX=-8.24091 CenterY=-197.481 CenterZ=0 NormalX=0 NormalY=0 NormalZ=1 AngleXU=0 Radius=1
    g19: Circle CenterX=12.8789 CenterY=-141.321 CenterZ=0 NormalX=0 NormalY=0 NormalZ=1 AngleXU=0 Radius=1
    g20: BSplineCurve PolesCount=3 KnotsCount=2 Degree=2 IsPeriodic=0
    g21: GeomPoint X=-195.441 Y=-127.082 Z=0
    g22: GeomPoint X=12.8789 Y=-141.321 Z=0
    g23: Circle CenterX=-12.8016 CenterY=-179.036 CenterZ=0 NormalX=0 NormalY=0 NormalZ=1 AngleXU=0 Radius=10.5072
    g24: Circle CenterX=0.933922 CenterY=-166.43 CenterZ=0 NormalX=0 NormalY=0 NormalZ=1 AngleXU=0 Radius=3.26661
    g25: Circle CenterX=-33.5518 CenterY=-176.44 CenterZ=0 NormalX=0 NormalY=0 NormalZ=1 AngleXU=0 Radius=5.64388
    g26: Circle CenterX=-47.2366 CenterY=-173.859 CenterZ=0 NormalX=0 NormalY=0 NormalZ=1 AngleXU=0 Radius=3.01653
    g27: Circle CenterX=-56.2595 CenterY=-171.456 CenterZ=0 NormalX=0 NormalY=0 NormalZ=1 AngleXU=0 Radius=2.12826
    g28: ArcOfCircle CenterX=51.2151 CenterY=-198.473 CenterZ=0 NormalX=0 NormalY=0 NormalZ=1 AngleXU=0 Radius=20 StartAngle=2.78189 EndAngle=4.35269
    g29: LineSegment StartX=32.4951 StartY=-191.433 StartZ=0 EndX=94.6578 EndY=-26.1352 EndZ=0
    g30: LineSegment StartX=43.1192 StartY=-220.001 StartZ=0 EndX=-196.497 EndY=-129.89 EndZ=0
    g31: LineSegment StartX=43.1192 StartY=-220.001 StartZ=0 EndX=44.1752 EndY=-217.193 EndZ=0
    g32: LineSegment StartX=117.223 StartY=-19.0875 StartZ=0 EndX=117.223 EndY=-16.0875 EndZ=0
    g33: LineSegment StartX=117.223 StartY=-16.0875 StartZ=0 EndX=17.2232 EndY=-16.0875 EndZ=0
    g34: LineSegment StartX=17.2232 StartY=-16.0875 StartZ=0 EndX=17.2232 EndY=-19.0875 EndZ=0
    g35: LineSegment StartX=28.8094 StartY=-19.0875 StartZ=0 EndX=17.2232 EndY=-19.0875 EndZ=0
    g36: LineSegment StartX=47.0443 StartY=-50.4712 StartZ=0 EndX=12.8789 EndY=-141.321 EndZ=0
    g37: LineSegment StartX=-195.441 StartY=-127.082 StartZ=0 EndX=-196.497 EndY=-129.89 EndZ=0
    g38: LineSegment StartX=85.2866 StartY=-36.8766 StartZ=0 EndX=78.9396 EndY=-53.7463 EndZ=0
    g39: LineSegment StartX=60.9579 StartY=-27.7053 StartZ=0 EndX=54.6191 EndY=-44.5532 EndZ=0
    g40: LineSegment StartX=68.0907 StartY=-82.7664 StartZ=0 EndX=61.7465 EndY=-99.6365 EndZ=0
    g41: LineSegment StartX=43.7619 StartY=-73.595 StartZ=0 EndX=37.426 EndY=-90.4435 EndZ=0
    g42: LineSegment StartX=50.885 StartY=-128.652 StartZ=0 EndX=44.5456 EndY=-145.522 EndZ=0
    g43: LineSegment StartX=26.5562 StartY=-119.481 StartZ=0 EndX=20.2251 EndY=-136.329 EndZ=0
    g44: LineSegment StartX=9.3071 StartY=-165.349 StartZ=0 EndX=2.97115 EndY=-182.197 EndZ=0
    g45: LineSegment StartX=33.6358 StartY=-174.52 StartZ=0 EndX=27.2917 EndY=-191.39 EndZ=0
  constraints (71):
    c: Block(g0)
    c: Block(g1)
    c: Block(g2)
    c: Block(g4)
    c: Block(g3)
    c: Block(g6)
    c: Block(g5)
    c: Block(g8)
    c: Block(g7)
    c: Weight(g9) = 1
    c: Equal(g9,g10)
    c: Equal(g9,g11)
    c: Equal(g9,g12)
    c: InternalAlignment(g9-g12 -> g13) x4
    c: InternalAlignment(g14,g13)
    c: InternalAlignment(g15,g13)
    c: Block(g16)
    c: Weight(g17) = 1
    c: Equal(g17,g18)
    c: Equal(g17,g19)
    c: InternalAlignment(g17,g20)
    c: InternalAlignment(g18,g20)
    c: InternalAlignment(g19,g20)
    c: InternalAlignment(g21,g20)
    c: InternalAlignment(g22,g20)
    c: Block(g20)
    c: Block(g23)
    c: Block(g24)
    c: Block(g25)
    c: Block(g26)
    c: Block(g27)
    c: Block(g28)
    c: Coincident(g29,g28)
    c: Coincident(g29,g0)
    c: Block(g13)
    c: Coincident(g31,g30)
    c: Coincident(g31,g28)
    c: Block(g31)
    c: Coincident(g32,g0)
    c: Vertical(g32)
    c: Coincident(g33,g32)
    c: Horizontal(g33)
    c: Coincident(g34,g33)
    c: Vertical(g34)
    c: Block(g33)
    c: Coincident(g35,g13)
    c: Coincident(g35,g34)
    c: Horizontal(g35)
    c: Coincident(g36,g13)
    c: Coincident(g36,g20)
    c: Coincident(g37,g20)
    c: Coincident(g37,g30)
    c: Block(g30)
    c: Coincident(g38,g1)
    c: Coincident(g38,g2)
    c: Coincident(g39,g1)
    c: Coincident(g39,g2)
    c: Coincident(g40,g3)
    c: Coincident(g40,g4)
    c: Coincident(g41,g3)
    c: Coincident(g41,g4)
    c: Coincident(g42,g5)
    c: Coincident(g42,g6)
    c: Coincident(g43,g5)
    c: Coincident(g43,g6)
    c: Coincident(g44,g7)
    c: Coincident(g44,g8)
    c: Coincident(g45,g7)
    c: Coincident(g45,g8)
    c: Distance(g30) = 256
    c: Distance(g33) = 100
FEATURE [Part::Extrusion] Extrude002
  Base = -> Sketch001
  Dir = (1,0,0)
  DirMode = 2
  FaceMakerClass = Part::FaceMakerBullseye
  LengthFwd = 8
  LengthRev = 0
  Solid = true
  Symmetric = false
FEATURE [Sketcher::SketchObject] Sketch002
  FullyConstrained = true
  sketch-geometry (20):
    g0: LineSegment StartX=-2.77179 StartY=-200.304 StartZ=0 EndX=5.22821 EndY=-200.304 EndZ=0
    g1: LineSegment StartX=5.22821 StartY=-200.304 StartZ=0 EndX=5.22821 EndY=-197.304 EndZ=0
    g2: LineSegment StartX=-2.77179 StartY=-200.304 StartZ=0 EndX=-2.77179 EndY=-197.304 EndZ=0
    g3: LineSegment StartX=5.22821 StartY=-197.304 StartZ=0 EndX=8.22821 EndY=-197.304 EndZ=0
    g4: LineSegment StartX=-2.77179 StartY=-197.304 StartZ=0 EndX=-5.77179 EndY=-197.304 EndZ=0
    g5: LineSegment StartX=19.2282 StartY=-203.304 StartZ=0 EndX=19.2282 EndY=-206.304 EndZ=0
    g6: LineSegment StartX=-16.7718 StartY=-203.304 StartZ=0 EndX=-16.7718 EndY=-206.304 EndZ=0
    g7: LineSegment StartX=-16.7718 StartY=-206.304 StartZ=0 EndX=19.2282 EndY=-206.304 EndZ=0
    g8: Circle CenterX=-16.7718 CenterY=-203.304 CenterZ=0 NormalX=0 NormalY=0 NormalZ=1 AngleXU=0 Radius=1
    g9: Circle CenterX=-5.77179 CenterY=-203.304 CenterZ=0 NormalX=0 NormalY=0 NormalZ=1 AngleXU=0 Radius=1
    g10: Circle CenterX=-5.77179 CenterY=-197.304 CenterZ=0 NormalX=0 NormalY=0 NormalZ=1 AngleXU=0 Radius=1
    g11: BSplineCurve PolesCount=3 KnotsCount=2 Degree=2 IsPeriodic=0
    g12: GeomPoint X=-16.7718 Y=-203.304 Z=0
    g13: GeomPoint X=-5.77179 Y=-197.304 Z=0
    g14: Circle CenterX=19.2282 CenterY=-203.304 CenterZ=0 NormalX=0 NormalY=0 NormalZ=1 AngleXU=0 Radius=1
    g15: Circle CenterX=8.22821 CenterY=-203.304 CenterZ=0 NormalX=0 NormalY=0 NormalZ=1 AngleXU=0 Radius=1
    g16: Circle CenterX=8.22821 CenterY=-197.304 CenterZ=0 NormalX=0 NormalY=0 NormalZ=1 AngleXU=0 Radius=1
    g17: BSplineCurve PolesCount=3 KnotsCount=2 Degree=2 IsPeriodic=0
    g18: GeomPoint X=19.2282 Y=-203.304 Z=0
    g19: GeomPoint X=8.22821 Y=-197.304 Z=0
  constraints (41):
    c: Horizontal(g0)
    c: Distance(g0) = 8
    c: Coincident(g1,g0)
    c: Vertical(g1)
    c: Distance(g1) = 3
    c: Coincident(g2,g0)
    c: Vertical(g2)
    c: Distance(g2) = 3
    c: Coincident(g3,g1)
    c: Horizontal(g3)
    c: Distance(g3) = 3
    c: Coincident(g4,g2)
    c: Horizontal(g4)
    c: Distance(g4) = 3
    c: Vertical(g5)
    c: Vertical(g6)
    c: Coincident(g7,g6)
    c: Coincident(g7,g5)
    c: Weight(g8) = 1
    c: Equal(g8,g9)
    c: Equal(g8,g10)
    c: Coincident(g11,g4)
    c: InternalAlignment(g8,g11)
    c: InternalAlignment(g9,g11)
    c: InternalAlignment(g10,g11)
    c: InternalAlignment(g12,g11)
    c: InternalAlignment(g13,g11)
    c: Coincident(g17,g5)
    c: Weight(g14) = 1
    c: Equal(g14,g15)
    c: Equal(g14,g16)
    c: Coincident(g17,g3)
    c: InternalAlignment(g14,g17)
    c: InternalAlignment(g15,g17)
    c: InternalAlignment(g16,g17)
    c: InternalAlignment(g18,g17)
    c: InternalAlignment(g19,g17)
    c: Block(g7)
    c: Block(g17)
    c: Block(g11)
    c: Block(g6)
FEATURE [Part::Extrusion] Extrude003
  Base = -> Sketch002
  Dir = (0,0,1)
  DirMode = 2
  FaceMakerClass = Part::FaceMakerBullseye
  LengthFwd = 260
  LengthRev = 0
  Solid = true
  Symmetric = false
FEATURE [Part::Extrusion] Extrude
  Base = -> Sketch
  Dir = (0,0,1)
  DirMode = 2
  FaceMakerClass = Part::FaceMakerBullseye
  LengthFwd = 14
  LengthRev = 0
  Solid = true
  Symmetric = false
